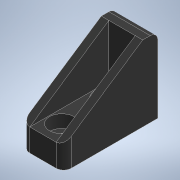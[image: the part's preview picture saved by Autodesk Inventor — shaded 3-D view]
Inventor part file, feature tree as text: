
AUTODESK INVENTOR PART (.ipt)
format: ipt  version: 2022.2 (Build 262287010, 287A)  size: 139,264 bytes
history: native  units: mm
features: sketch x3, extrude x2, hole x1, mirror x1, fillet x1
ambient origin geometry x8: Origin, YZ Plane, XZ Plane, XY Plane, X Axis, Y Axis, Z Axis, Center Point
bodies: Volumenkörper1 (feature_tree)
feature tree (8):
  extrude  "Extrusion1"  Depth=25.0mm
  hole  "Bohrung1"  [1 undecoded]
  extrude  "Extrusion2"  Depth=2.0mm
  mirror  "Spiegeln1"
  fillet  "Rundung2"  Radius=12.0mm
  sketch  "Skizze1"  dims[d0=20.0mm d1=25.0mm]
  sketch  "Skizze2"  dims[d2=4.0mm d3=6.0mm]
  sketch  "Skizze3"  dims[d4=11.0mm d5=0.0mm d6=5.0mm d7=3.4mm d8=6.0mm d9=6.5mm d10=3.4mm d11=90.0deg d12=8.0mm d13=20.594885mm d14=12.0mm d15=2.0mm d16=0.0mm d18=2.0mm]
note: 1 required parameter value undecoded (feature->parameter linkage not recoverable at this tier; creation-order binding heuristic only, values carry confidence <= 0.55)
